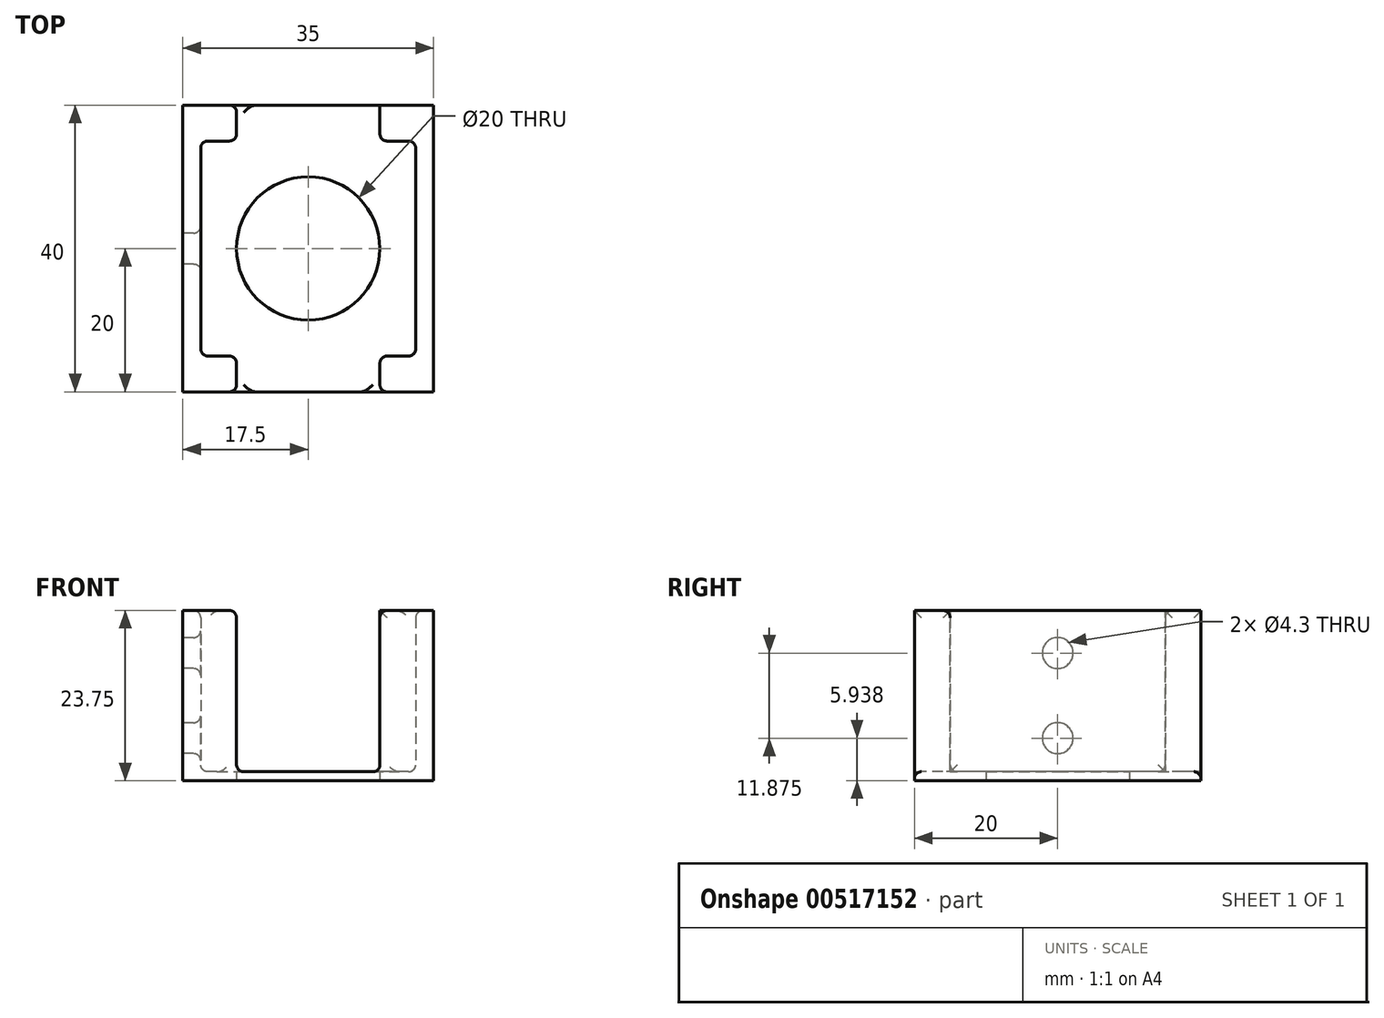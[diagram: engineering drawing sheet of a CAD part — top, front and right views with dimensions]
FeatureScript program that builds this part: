
annotation { "Feature Type Name" : "Feature", "Feature Type Description" : "" }
export const myFeature = defineFeature(function(context is Context, id is Id, definition is map)
    precondition{}
    {
        {
            var Q0;
            Q0=qCreatedBy(makeId("Top.planeOp"),FACE);
            var sketch = newSketch(context, id + "F0", { "sketchPlane" : qUnion([Q0])});
            skLineSegment(sketch, "E0.bottom", {"start": v(20, 20) * mm, "end": v(-20, 20) * mm});
            skLineSegment(sketch, "E0.top", {"start": v(20, -20) * mm, "end": v(-20, -20) * mm});
            skLineSegment(sketch, "E0.left", {"start": v(20, 20) * mm, "end": v(20, -20) * mm});
            skLineSegment(sketch, "E0.right", {"start": v(-20, 20) * mm, "end": v(-20, -20) * mm});
            skPoint(sketch, "E0.middle", {"position": v(0, 0) * mm});
            skLineSegment(sketch, "E1.bottom", {"start": v(15, 15) * mm, "end": v(-15, 15) * mm});
            skLineSegment(sketch, "E1.top", {"start": v(15, -15) * mm, "end": v(-15, -15) * mm});
            skLineSegment(sketch, "E1.left", {"start": v(15, 15) * mm, "end": v(15, -15) * mm});
            skLineSegment(sketch, "E1.right", {"start": v(-15, 15) * mm, "end": v(-15, -15) * mm});
            skSolve(sketch);
        }
        {
            var Q0;
            Q0=makeQuery(id+"F0.imprint","IMPRINT",FACE,{"disambiguationData":[TD([[makeQuery(id+"F0.imprint","IMPRINT",EDGE,{"derivedFrom":sQuery(id+"F0.wireOp",EDGE,"E0.bottom")}),1.0]])]});
            extrude(context, id + "F1", {"entities" : qUnion([Q0]), "depth" : 25 * mm, "offsetDistance" : 25 * mm});
        }
        {
            var Q0;
            Q0=makeQuery(id+"F1.opExtrude","SWEPT_FACE",FACE,{"disambiguationData":[OSD([sQuery(id+"F0.wireOp",EDGE,"E0.top")])]});
            var sketch = newSketch(context, id + "F2", { "sketchPlane" : qUnion([Q0])});
            skLineSegment(sketch, "E2.bottom", {"start": v(-10, 2.5) * mm, "end": v(10, 2.5) * mm});
            skLineSegment(sketch, "E2.top", {"start": v(-10, 22.5) * mm, "end": v(10, 22.5) * mm});
            skLineSegment(sketch, "E2.left", {"start": v(-10, 2.5) * mm, "end": v(-10, 22.5) * mm});
            skLineSegment(sketch, "E2.right", {"start": v(10, 2.5) * mm, "end": v(10, 22.5) * mm});
            skPoint(sketch, "E2.middle", {"position": v(0, 12.5) * mm});
            skPoint(sketch, "E2.middle.positionSnap0", {"position": v(0, 25) * mm});
            skPoint(sketch, "E2.middle.positionSnap1", {"position": v(-20, 12.5) * mm});
            skPoint(sketch, "E2.centerSnap0", {"position": v(0, 25) * mm});
            skPoint(sketch, "E2.centerSnap1", {"position": v(-20, 12.5) * mm});
            skSolve(sketch);
        }
        {
            var Q0;
            Q0=makeQuery(id+"F2.imprint","IMPRINT",FACE,{"disambiguationData":[TD([[makeQuery(id+"F2.imprint","IMPRINT",EDGE,{"derivedFrom":sQuery(id+"F2.wireOp",EDGE,"E2.bottom")}),1.0]])]});
            extrude(context, id + "F3", {"entities" : qUnion([Q0]), "operationType" : NewBodyOperationType.REMOVE, "endBound" : BoundingType.THROUGH_ALL, "oppositeDirection" : true, "depth" : 25 * mm, "offsetDistance" : 25 * mm});
        }
        {
            var Q0;
            Q0=makeQuery(id+"F1.opExtrude","CAP_FACE",FACE,{"disambiguationData":[OSD([sQuery(id+"F0.wireOp",EDGE,"E0.bottom"),sQuery(id+"F0.wireOp",EDGE,"E0.top"),sQuery(id+"F0.wireOp",EDGE,"E0.left"),sQuery(id+"F0.wireOp",EDGE,"E0.right"),sQuery(id+"F0.wireOp",EDGE,"E1.bottom"),sQuery(id+"F0.wireOp",EDGE,"E1.top"),sQuery(id+"F0.wireOp",EDGE,"E1.left"),sQuery(id+"F0.wireOp",EDGE,"E1.right")])],"isStart":true});
            var sketch = newSketch(context, id + "F4", { "sketchPlane" : qUnion([Q0])});
            skLineSegment(sketch, "E3.bottom", {"start": v(-20, 20) * mm, "end": v(20, 20) * mm});
            skLineSegment(sketch, "E3.top", {"start": v(-20, -20) * mm, "end": v(20, -20) * mm});
            skLineSegment(sketch, "E3.left", {"start": v(-20, 20) * mm, "end": v(-20, -20) * mm});
            skLineSegment(sketch, "E3.right", {"start": v(20, 20) * mm, "end": v(20, -20) * mm});
            skSolve(sketch);
        }
        {
            var Q0;
            Q0=makeQuery(id+"F4.imprint","IMPRINT",FACE,{"disambiguationData":[TD([[makeQuery(id+"F4.imprint","IMPRINT",EDGE,{"derivedFrom":makeQuery(id+"F1.opExtrude","CAP_EDGE",EDGE,{"disambiguationData":[OSD([sQuery(id+"F0.wireOp",EDGE,"E1.bottom")])],"isStart":true})}),-1.0]])]});
            var Q1;
            Q1=makeQuery(id+"F4.imprint","IMPRINT",FACE,{"disambiguationData":[TD([[makeQuery(id+"F4.imprint","IMPRINT",EDGE,{"derivedFrom":sQuery(id+"F4.wireOp",EDGE,"E3.bottom")}),1.0]])]});
            extrude(context, id + "F5", {"entities" : qUnion([Q0, Q1]), "operationType" : NewBodyOperationType.ADD, "depth" : 1.25 * mm, "offsetDistance" : 25 * mm});
        }
        {
            var Q0;
            Q0=makeQuery(id+"F5.opExtrude","CAP_FACE",FACE,{"disambiguationData":[OSD([sQuery(id+"F4.wireOp",EDGE,"E3.bottom"),sQuery(id+"F4.wireOp",EDGE,"E3.top"),sQuery(id+"F4.wireOp",EDGE,"E3.left"),sQuery(id+"F4.wireOp",EDGE,"E3.right")])],"isStart":false});
            var sketch = newSketch(context, id + "F6", { "sketchPlane" : qUnion([Q0])});
            skCircle(sketch, "E4", {"center": v(0, 0) * mm, "radius": 10 * mm});
            skSolve(sketch);
        }
        {
            var Q0;
            Q0=makeQuery(id+"F6.imprint","IMPRINT",FACE,{"disambiguationData":[TD([[makeQuery(id+"F6.imprint","IMPRINT",EDGE,{"derivedFrom":sQuery(id+"F6.wireOp",EDGE,"E4")}),1.0]])]});
            extrude(context, id + "F7", {"entities" : qUnion([Q0]), "operationType" : NewBodyOperationType.REMOVE, "endBound" : BoundingType.THROUGH_ALL, "oppositeDirection" : true, "depth" : 25 * mm, "offsetDistance" : 25 * mm});
        }
        {
            var Q0;
            Q0=makeQuery(id+"F5.boolean.opBoolean","MERGE",FACE,{"derivedFrom":[makeQuery(id+"F1.opExtrude","SWEPT_FACE",FACE,{"disambiguationData":[OSD([sQuery(id+"F0.wireOp",EDGE,"E0.top")])]}),makeQuery(id+"F5.opExtrude","SWEPT_FACE",FACE,{"disambiguationData":[OSD([sQuery(id+"F4.wireOp",EDGE,"E3.bottom")])]})]});
            var sketch = newSketch(context, id + "F8", { "sketchPlane" : qUnion([Q0])});
            skLineSegment(sketch, "E5", {"start": v(-20, 22.5) * mm, "end": v(20, 22.5) * mm});
            skSolve(sketch);
        }
        {
            var Q0;
            {var subQ0=sQuery(id+"F0.wireOp",EDGE,"E0.top");var subQ1=makeQuery(id+"F1.opExtrude","CAP_EDGE",EDGE,{"disambiguationData":[OSD([subQ0])],"isStart":false});Q0=makeQuery(id+"F8.imprint","IMPRINT",FACE,{"disambiguationData":[TD([[makeQuery(id+"F8.imprint","IMPRINT",EDGE,{"derivedFrom":subQ1}),1.0]])]});}
            extrude(context, id + "F9", {"entities" : qUnion([Q0]), "operationType" : NewBodyOperationType.REMOVE, "endBound" : BoundingType.THROUGH_ALL, "oppositeDirection" : true, "depth" : 25 * mm, "offsetDistance" : 25 * mm});
        }
        {
            var Q0;
            Q0=makeQuery(id+"F3.boolean.opBoolean","COPY",FACE,{"disambiguationData":[TD([makeQuery(id+"F1.opExtrude","SWEPT_FACE",FACE,{"disambiguationData":[OSD([sQuery(id+"F0.wireOp",EDGE,"E0.bottom")])]})])],"derivedFrom":makeQuery(id+"F3.opExtrude","SWEPT_FACE",FACE,{"disambiguationData":[OSD([sQuery(id+"F2.wireOp",EDGE,"E2.bottom")])]})});
            var Q1;
            Q1=makeQuery(id+"F3.boolean.opBoolean","COPY",FACE,{"disambiguationData":[TD([makeQuery(id+"F1.opExtrude","SWEPT_FACE",FACE,{"disambiguationData":[OSD([sQuery(id+"F0.wireOp",EDGE,"E0.top")])]})])],"derivedFrom":makeQuery(id+"F3.opExtrude","SWEPT_FACE",FACE,{"disambiguationData":[OSD([sQuery(id+"F2.wireOp",EDGE,"E2.bottom")])]})});
            extrude(context, id + "F10", {"entities" : qUnion([Q0, Q1]), "operationType" : NewBodyOperationType.REMOVE, "oppositeDirection" : true, "depth" : 2.5 * mm, "offsetDistance" : 25 * mm});
        }
        {
            var Q0;
            Q0=makeQuery(id+"F9.boolean.opBoolean","COPY",FACE,{"disambiguationData":[TD([makeQuery(id+"F1.opExtrude","SWEPT_FACE",FACE,{"disambiguationData":[OSD([sQuery(id+"F0.wireOp",EDGE,"E0.right")])]})])],"derivedFrom":makeQuery(id+"F9.opExtrude","SWEPT_FACE",FACE,{"disambiguationData":[OSD([sQuery(id+"F8.wireOp",EDGE,"E5")])]})});
            var sketch = newSketch(context, id + "F11", { "sketchPlane" : qUnion([Q0])});
            skLineSegment(sketch, "E6", {"start": v(-17.5, -20) * mm, "end": v(-17.5, 20) * mm});
            skSolve(sketch);
        }
        {
            var Q0;
            Q0=makeQuery(id+"F9.boolean.opBoolean","COPY",FACE,{"disambiguationData":[TD([makeQuery(id+"F1.opExtrude","SWEPT_FACE",FACE,{"disambiguationData":[OSD([sQuery(id+"F0.wireOp",EDGE,"E0.left")])]})])],"derivedFrom":makeQuery(id+"F9.opExtrude","SWEPT_FACE",FACE,{"disambiguationData":[OSD([sQuery(id+"F8.wireOp",EDGE,"E5")])]})});
            var sketch = newSketch(context, id + "F12", { "sketchPlane" : qUnion([Q0])});
            skLineSegment(sketch, "E7", {"start": v(17.5, -20) * mm, "end": v(17.5, 20) * mm});
            skSolve(sketch);
        }
        {
            var Q0;
            {var subQ0=sQuery(id+"F11.wireOp",EDGE,"E6");Q0=makeQuery(id+"F11.imprint","IMPRINT",FACE,{"disambiguationData":[TD([[makeQuery(id+"F11.imprint","IMPRINT",EDGE,{"derivedFrom":subQ0}),1.0]])]});}
            var Q1;
            {var subQ0=sQuery(id+"F12.wireOp",EDGE,"E7");Q1=makeQuery(id+"F12.imprint","IMPRINT",FACE,{"disambiguationData":[TD([[makeQuery(id+"F12.imprint","IMPRINT",EDGE,{"derivedFrom":subQ0}),-1.0]])]});}
            extrude(context, id + "F13", {"entities" : qUnion([Q0, Q1]), "operationType" : NewBodyOperationType.REMOVE, "endBound" : BoundingType.THROUGH_ALL, "oppositeDirection" : true, "depth" : 25 * mm, "offsetDistance" : 25 * mm});
        }
        {
            var Q0;
            Q0=makeQuery(id+"F13.boolean.opBoolean","COPY",FACE,{"derivedFrom":makeQuery(id+"F13.opExtrude","SWEPT_FACE",FACE,{"disambiguationData":[OSD([sQuery(id+"F11.wireOp",EDGE,"E6")])]})});
            var sketch = newSketch(context, id + "F14", { "sketchPlane" : qUnion([Q0])});
            skPoint(sketch, "E8.startSnap0", {"position": v(0, 22.5) * mm});
            skPoint(sketch, "E8.startSnap1", {"position": v(-20, 10.62) * mm});
            skCircle(sketch, "E9", {"center": v(0, 16.56) * mm, "radius": 2.15 * mm});
            skCircle(sketch, "E10", {"center": v(0, 4.69) * mm, "radius": 2.15 * mm});
            skSolve(sketch);
        }
        {
            var Q0;
            Q0=makeQuery(id+"F14.imprint","IMPRINT",FACE,{"disambiguationData":[TD([[makeQuery(id+"F14.imprint","IMPRINT",EDGE,{"derivedFrom":sQuery(id+"F14.wireOp",EDGE,"E9")}),1.0]])]});
            var Q1;
            Q1=makeQuery(id+"F14.imprint","IMPRINT",FACE,{"disambiguationData":[TD([[makeQuery(id+"F14.imprint","IMPRINT",EDGE,{"derivedFrom":sQuery(id+"F14.wireOp",EDGE,"E10")}),1.0]])]});
            extrude(context, id + "F15", {"entities" : qUnion([Q0, Q1]), "operationType" : NewBodyOperationType.REMOVE, "oppositeDirection" : true, "depth" : 2.5 * mm, "offsetDistance" : 25 * mm});
        }
        {
            var Q0;
            {var subQ0=makeQuery(id+"F1.opExtrude","SWEPT_FACE",FACE,{"disambiguationData":[OSD([sQuery(id+"F0.wireOp",EDGE,"E0.top")])]});var subQ1=sQuery(id+"F2.wireOp",EDGE,"E2.bottom");var subQ4=sQuery(id+"F2.wireOp",EDGE,"E2.left");var subQ5=makeQuery(id+"F3.opExtrude","SWEPT_FACE",FACE,{"disambiguationData":[OSD([subQ4])]});Q0=makeQuery(id+"F10.boolean.opBoolean","MERGE",FACE,{"derivedFrom":[makeQuery(id+"F3.boolean.opBoolean","COPY",FACE,{"disambiguationData":[TD([subQ0])],"derivedFrom":subQ5}),makeQuery(id+"F10.opExtrude","SWEPT_FACE",FACE,{"disambiguationData":[OSD([subQ1,subQ4]),TDD([makeQuery(id+"F3.boolean.opBoolean","COPY",EDGE,{"disambiguationData":[TD([subQ0])],"derivedFrom":makeQuery(id+"F3.opExtrude","SWEPT_EDGE",EDGE,{"disambiguationData":[OSD([subQ1,subQ4])]})})])]})]});}
            var Q1;
            {var subQ0=makeQuery(id+"F1.opExtrude","SWEPT_FACE",FACE,{"disambiguationData":[OSD([sQuery(id+"F0.wireOp",EDGE,"E0.bottom")])]});var subQ2=sQuery(id+"F2.wireOp",EDGE,"E2.bottom");var subQ4=sQuery(id+"F2.wireOp",EDGE,"E2.left");var subQ5=makeQuery(id+"F3.opExtrude","SWEPT_FACE",FACE,{"disambiguationData":[OSD([subQ4])]});Q1=makeQuery(id+"F10.boolean.opBoolean","MERGE",FACE,{"derivedFrom":[makeQuery(id+"F3.boolean.opBoolean","COPY",FACE,{"disambiguationData":[TD([subQ0])],"derivedFrom":subQ5}),makeQuery(id+"F10.opExtrude","SWEPT_FACE",FACE,{"disambiguationData":[OSD([subQ2,subQ4]),TDD([makeQuery(id+"F3.boolean.opBoolean","COPY",EDGE,{"disambiguationData":[TD([subQ0])],"derivedFrom":makeQuery(id+"F3.opExtrude","SWEPT_EDGE",EDGE,{"disambiguationData":[OSD([subQ2,subQ4])]})})])]})]});}
            var Q2;
            {var subQ0=makeQuery(id+"F1.opExtrude","SWEPT_FACE",FACE,{"disambiguationData":[OSD([sQuery(id+"F0.wireOp",EDGE,"E0.top")])]});var subQ1=sQuery(id+"F2.wireOp",EDGE,"E2.bottom");var subQ3=sQuery(id+"F2.wireOp",EDGE,"E2.right");var subQ4=makeQuery(id+"F3.opExtrude","SWEPT_FACE",FACE,{"disambiguationData":[OSD([subQ3])]});Q2=makeQuery(id+"F10.boolean.opBoolean","MERGE",FACE,{"derivedFrom":[makeQuery(id+"F3.boolean.opBoolean","COPY",FACE,{"disambiguationData":[TD([subQ0])],"derivedFrom":subQ4}),makeQuery(id+"F10.opExtrude","SWEPT_FACE",FACE,{"disambiguationData":[OSD([subQ1,subQ3]),TDD([makeQuery(id+"F3.boolean.opBoolean","COPY",EDGE,{"disambiguationData":[TD([subQ0])],"derivedFrom":makeQuery(id+"F3.opExtrude","SWEPT_EDGE",EDGE,{"disambiguationData":[OSD([subQ1,subQ3])]})})])]})]});}
            var Q3;
            {var subQ0=sQuery(id+"F2.wireOp",EDGE,"E2.bottom");var subQ1=sQuery(id+"F2.wireOp",EDGE,"E2.right");Q3=makeQuery(id+"F10.boolean.opBoolean","COPY",EDGE,{"derivedFrom":makeQuery(id+"F10.opExtrude","CAP_EDGE",EDGE,{"disambiguationData":[OSD([subQ0,subQ1]),TDD([makeQuery(id+"F3.boolean.opBoolean","COPY",EDGE,{"disambiguationData":[TD([makeQuery(id+"F1.opExtrude","SWEPT_FACE",FACE,{"disambiguationData":[OSD([sQuery(id+"F0.wireOp",EDGE,"E0.bottom")])]})])],"derivedFrom":makeQuery(id+"F3.opExtrude","SWEPT_EDGE",EDGE,{"disambiguationData":[OSD([subQ0,subQ1])]})})])],"isStart":false})});}
            var Q4;
            {var subQ2=makeQuery(id+"F1.opExtrude","SWEPT_FACE",FACE,{"disambiguationData":[OSD([sQuery(id+"F0.wireOp",EDGE,"E1.bottom")])]});var subQ9=makeQuery(id+"F1.opExtrude","SWEPT_FACE",FACE,{"disambiguationData":[OSD([sQuery(id+"F0.wireOp",EDGE,"E1.left")])]});Q4=makeQuery(id+"F10.boolean.opBoolean","SPLIT",FACE,{"disambiguationData":[TD([subQ9])],"derivedFrom":subQ2});}
            var Q5;
            Q5=makeQuery(id+"F1.opExtrude","SWEPT_FACE",FACE,{"disambiguationData":[OSD([sQuery(id+"F0.wireOp",EDGE,"E1.left")])]});
            var Q6;
            Q6=makeQuery(id+"F1.opExtrude","SWEPT_FACE",FACE,{"disambiguationData":[OSD([sQuery(id+"F0.wireOp",EDGE,"E1.right")])]});
            fillet(context, id + "F16", {"entities" : qUnion([Q0, Q1, Q2, Q3, Q4, Q5, Q6]), "radius" : 1 * mm, "tangentPropagation" : true, "allowEdgeOverflow" : false});
        }
    });
